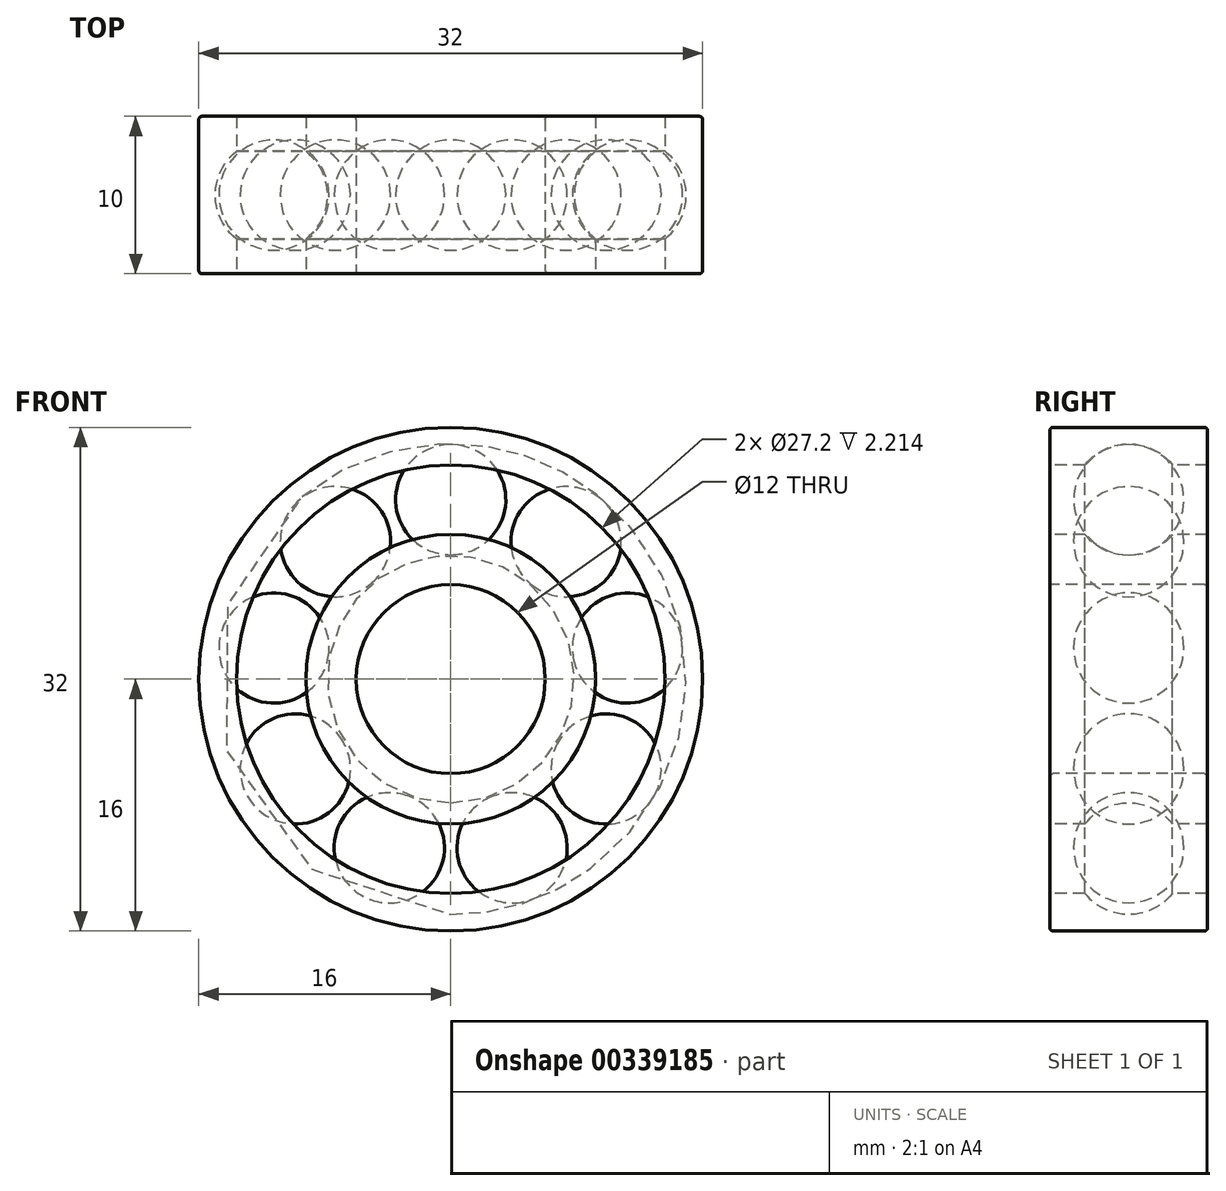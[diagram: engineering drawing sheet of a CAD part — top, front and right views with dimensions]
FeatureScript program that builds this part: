
annotation { "Feature Type Name" : "Feature", "Feature Type Description" : "" }
export const myFeature = defineFeature(function(context is Context, id is Id, definition is map)
    precondition{}
    {
        {
            var Q0;
            Q0=qCreatedBy(makeId("Right.planeOp"),FACE);
            var sketch = newSketch(context, id + "F0", { "sketchPlane" : qUnion([Q0])});
            skLineSegment(sketch, "E0", {"start": v(2.79, 13.6) * mm, "end": v(5, 13.6) * mm});
            skLineSegment(sketch, "E1", {"start": v(5, 13.6) * mm, "end": v(5, 15.8) * mm});
            skLineSegment(sketch, "E2", {"start": v(0, 6) * mm, "end": v(4.8, 6) * mm});
            skLineSegment(sketch, "E3", {"start": v(5, 6.2) * mm, "end": v(5, 9.2) * mm});
            skLineSegment(sketch, "E4", {"start": v(5, 9.2) * mm, "end": v(2.79, 9.2) * mm});
            skLineSegment(sketch, "E5", {"start": v(0, 16) * mm, "end": v(4.8, 16) * mm});
            skLineSegment(sketch, "E6.MirrorCS", {"start": v(-5, 13.6) * mm, "end": v(-5, 15.8) * mm});
            skLineSegment(sketch, "E7.MirrorCS", {"start": v(-2.79, 13.6) * mm, "end": v(-5, 13.6) * mm});
            skLineSegment(sketch, "E8.MirrorCS", {"start": v(-5, 9.2) * mm, "end": v(-2.79, 9.2) * mm});
            skLineSegment(sketch, "E9.MirrorCS", {"start": v(0, 16) * mm, "end": v(-4.8, 16) * mm});
            skLineSegment(sketch, "E10.MirrorCS", {"start": v(0, 6) * mm, "end": v(-4.8, 6) * mm});
            skLineSegment(sketch, "E11.MirrorCS", {"start": v(-5, 6.2) * mm, "end": v(-5, 9.2) * mm});
            skLineSegment(sketch, "E12", {"start": v(0, 0) * mm, "end": v(4.64, 0) * mm});
            skArc(sketch, "E13", {"start": v(-2.79, 9.2) * mm, "mid": v(0, 7.85) * mm, "end": v(2.79, 9.2) * mm});
            skArc(sketch, "E14.trimOffspring", {"start": v(2.79, 13.6) * mm, "mid": v(0, 14.95) * mm, "end": v(-2.79, 13.6) * mm});
            skPoint(sketch, "E15.visualSharp", {"position": v(-5, 16) * mm});
            skArc(sketch, "E15.filletArc", {"start": v(-4.8, 16) * mm, "mid": v(-4.94, 15.94) * mm, "end": v(-5, 15.8) * mm});
            skPoint(sketch, "E16.visualSharp", {"position": v(5, 16) * mm});
            skArc(sketch, "E16.filletArc", {"start": v(5, 15.8) * mm, "mid": v(4.94, 15.94) * mm, "end": v(4.8, 16) * mm});
            skPoint(sketch, "E17.visualSharp", {"position": v(5, 6) * mm});
            skArc(sketch, "E17.filletArc", {"start": v(4.8, 6) * mm, "mid": v(4.94, 6.06) * mm, "end": v(5, 6.2) * mm});
            skPoint(sketch, "E18.visualSharp", {"position": v(-5, 6) * mm});
            skArc(sketch, "E18.filletArc", {"start": v(-5, 6.2) * mm, "mid": v(-4.94, 6.06) * mm, "end": v(-4.8, 6) * mm});
            skSolve(sketch);
        }
        {
            var Q0;
            Q0 = qSketchRegion(id + "F0", true);
            var Q1;
            Q1=sQuery(id+"F0.wireOp",EDGE,"E12");
            revolve(context, id + "F1", {"entities" : qUnion([Q0]), "axis" : qUnion([Q1]), "revolveType" : RevolveType.FULL});
        }
        {
            var Q0;
            Q0=qCreatedBy(makeId("Right.planeOp"),FACE);
            var sketch = newSketch(context, id + "F2", { "sketchPlane" : qUnion([Q0])});
            skCircle(sketch, "E19", {"center": v(0, 11.4) * mm, "radius": 3.5 * mm});
            skLineSegment(sketch, "E20", {"start": v(0, 14.9) * mm, "end": v(0, 7.9) * mm});
            skSolve(sketch);
        }
        {
            var Q0;
            {var subQ0=sQuery(id+"F2.wireOp",EDGE,"E20");Q0=makeQuery(id+"F2.imprint","IMPRINT",FACE,{"disambiguationData":[TD([[makeQuery(id+"F2.imprint","IMPRINT",EDGE,{"derivedFrom":subQ0}),-1.0]])]});}
            var Q1;
            Q1=sQuery(id+"F2.wireOp",EDGE,"E20");
            revolve(context, id + "F3", {"entities" : qUnion([Q0]), "axis" : qUnion([Q1]), "revolveType" : RevolveType.FULL});
        }
        {
            var Q0;
            Q0=qCreatedBy(makeId("Right.planeOp"),FACE);
            var sketch = newSketch(context, id + "F4", { "sketchPlane" : qUnion([Q0])});
            skLineSegment(sketch, "E21", {"start": v(0, 0) * mm, "end": v(8.4, 0) * mm});
            skSolve(sketch);
        }
        {
            var Q0;
            Q0=makeQuery(id+"F3.opRevolve","SWEPT_BODY",BODY,{"disambiguationData":[OSD([sQuery(id+"F2.wireOp",EDGE,"E19"),sQuery(id+"F2.wireOp",EDGE,"E20")])]});
            var Q1;
            Q1=sQuery(id+"F4.wireOp",EDGE,"E21");
            circularPattern(context, id + "F5", {"entities" : qUnion([Q0]), "axis" : qUnion([Q1]), "angle" : 360 * degree, "instanceCount" : 9, "equalSpace" : true});
        }
    });
